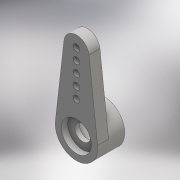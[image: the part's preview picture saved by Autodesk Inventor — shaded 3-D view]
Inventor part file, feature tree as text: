
AUTODESK INVENTOR PART (.ipt)
format: ipt  version: 2016 SP2 (Build 200236200, 236)  size: 162,304 bytes
history: native  units: mm
features: sketch x5, extrude x4, hole x1
ambient origin geometry x8: Origin, YZ Plane, XZ Plane, XY Plane, X Axis, Y Axis, Z Axis, Center Point
bodies: Solid1 (feature_tree)
feature tree (10):
  extrude  "Extrusion1"  Depth=17.3mm
  extrude  "Extrusion2"  Depth=1.75mm TaperAngle=0.0deg
  extrude  "Extrusion3"  Depth=2.55mm TaperAngle=0.0deg
  extrude  "Extrusion4"  Depth=1.0mm TaperAngle=0.0deg
  hole  "Hole1"  [1 undecoded]
  sketch  "Sketch1"  dims[d0=6.75mm d1=17.3mm]
  sketch  "Sketch2"  dims[d2=4.0mm d3=1.75mm d4=0.0mm]
  sketch  "Sketch3"  dims[d5=5.75mm d6=2.55mm d7=0.0mm]
  sketch  "Sketch4"  dims[d8=4.75mm d9=1.0mm d10=0.0mm]
  sketch  "Sketch5"  dims[d11=2.5mm d12=3.5mm d13=0.0mm d20=1.0mm d21=6.0mm d22=4.0mm d23=2.0mm d24=90.0deg d25=8.0mm d26=20.594885mm]
note: 1 required parameter value undecoded (feature->parameter linkage not recoverable at this tier; creation-order binding heuristic only, values carry confidence <= 0.55)
